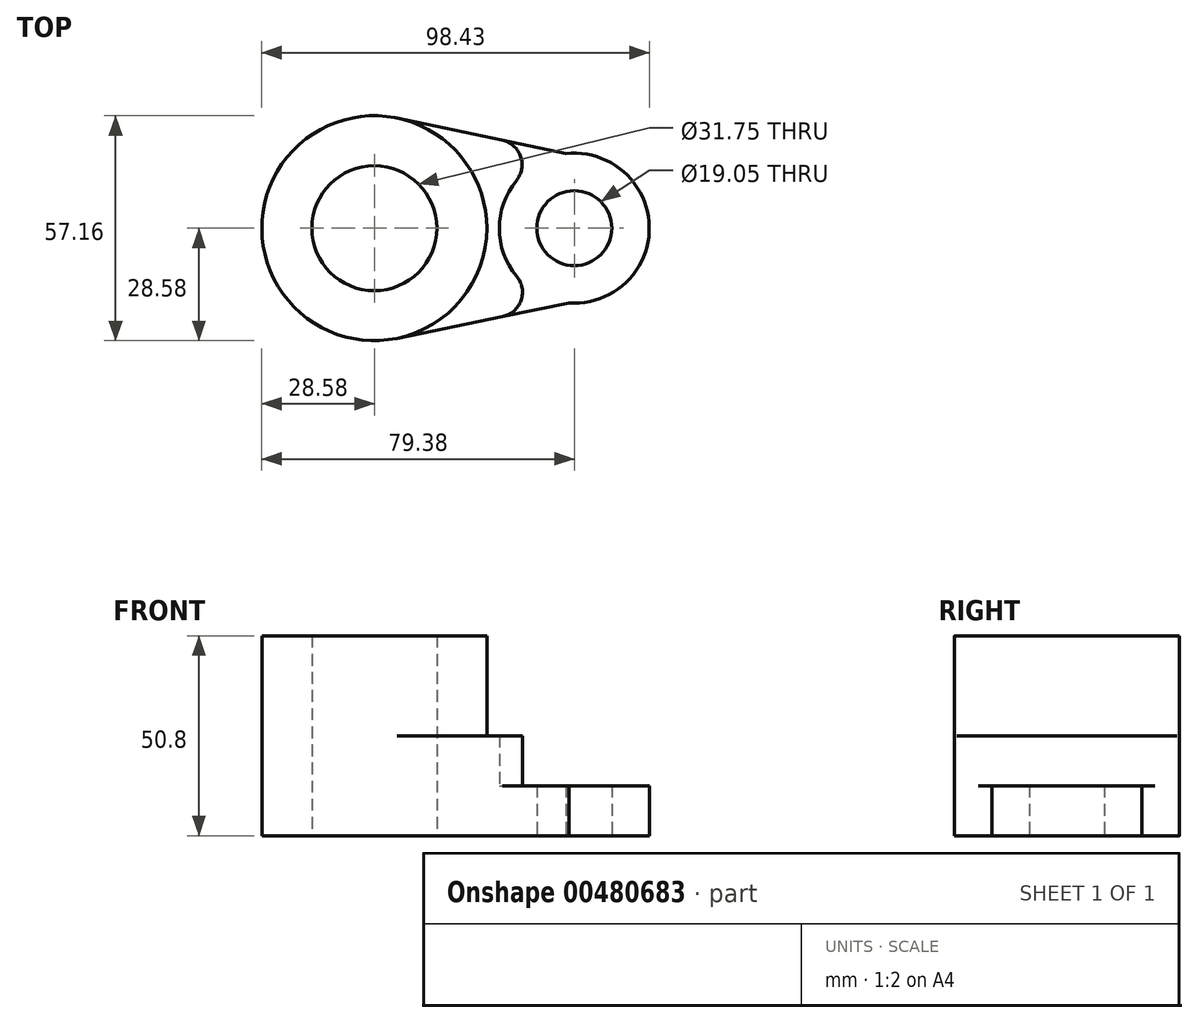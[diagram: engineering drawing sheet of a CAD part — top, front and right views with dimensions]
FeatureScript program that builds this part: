
annotation { "Feature Type Name" : "Feature", "Feature Type Description" : "" }
export const myFeature = defineFeature(function(context is Context, id is Id, definition is map)
    precondition{}
    {
        {
            var Q0;
            Q0=qCreatedBy(makeId("Top.planeOp"),FACE);
            var sketch = newSketch(context, id + "F0", { "sketchPlane" : qUnion([Q0])});
            skCircle(sketch, "E0", {"center": v(27.06, 0) * mm, "radius": 9.53 * mm});
            skCircle(sketch, "E1", {"center": v(27.06, 0) * mm, "radius": 19.05 * mm});
            skCircle(sketch, "E2", {"center": v(-23.74, 0) * mm, "radius": 15.88 * mm});
            skCircle(sketch, "E3", {"center": v(-23.74, 0) * mm, "radius": 28.58 * mm});
            skPoint(sketch, "E4", {"position": v(-14.86, 27.16) * mm});
            skPoint(sketch, "E5", {"position": v(24.93, 18.93) * mm});
            skLineSegment(sketch, "E6", {"start": v(-17.99, -27.99) * mm, "end": v(25.73, -19) * mm});
            skLineSegment(sketch, "E7", {"start": v(-17.84, 27.96) * mm, "end": v(24.93, 18.93) * mm});
            skSolve(sketch);
        }
        {
            var Q0;
            Q0=makeQuery(id+"F0.imprint","IMPRINT",FACE,{"disambiguationData":[TD([[makeQuery(id+"F0.imprint","IMPRINT",EDGE,{"derivedFrom":sQuery(id+"F0.wireOp",EDGE,"E2")}),-1.0]])]});
            extrude(context, id + "F1", {"entities" : qUnion([Q0]), "depth" : 50.8 * mm});
        }
        {
            var Q0;
            {var subQ0=sQuery(id+"F0.wireOp",EDGE,"E6");Q0=makeQuery(id+"F0.imprint","IMPRINT",FACE,{"disambiguationData":[TD([[makeQuery(id+"F0.imprint","IMPRINT",EDGE,{"derivedFrom":subQ0}),1.0]])]});}
            extrude(context, id + "F2", {"entities" : qUnion([Q0]), "operationType" : NewBodyOperationType.ADD, "depth" : 25.4 * mm});
        }
        {
            var Q0;
            Q0=makeQuery(id+"F0.imprint","IMPRINT",FACE,{"disambiguationData":[TD([[makeQuery(id+"F0.imprint","IMPRINT",EDGE,{"derivedFrom":sQuery(id+"F0.wireOp",EDGE,"E0")}),-1.0]])]});
            extrude(context, id + "F3", {"entities" : qUnion([Q0]), "operationType" : NewBodyOperationType.ADD, "depth" : 12.7 * mm});
        }
        {
            var Q0;
            {var subQ0=sQuery(id+"F0.wireOp",EDGE,"E1");var subQ1=sQuery(id+"F0.wireOp",EDGE,"E6");Q0=makeQuery(id+"F3.boolean.opBoolean","SPLIT",EDGE,{"disambiguationData":[topologyDisambiguationEdgeConnected([makeQuery(id+"F2.opExtrude","SWEPT_FACE",FACE,{"disambiguationData":[OSD([subQ0])]})])],"derivedFrom":makeQuery(id+"F2.opExtrude","SWEPT_EDGE",EDGE,{"disambiguationData":[OSD([subQ0,subQ1])]})});}
            var Q1;
            {var subQ0=sQuery(id+"F0.wireOp",EDGE,"E1");var subQ1=sQuery(id+"F0.wireOp",EDGE,"E7");Q1=makeQuery(id+"F3.boolean.opBoolean","SPLIT",EDGE,{"disambiguationData":[topologyDisambiguationEdgeConnected([makeQuery(id+"F2.opExtrude","SWEPT_FACE",FACE,{"disambiguationData":[OSD([subQ0])]})])],"derivedFrom":makeQuery(id+"F2.opExtrude","SWEPT_EDGE",EDGE,{"disambiguationData":[OSD([subQ0,subQ1])]})});}
            fillet(context, id + "F4", {"entities" : qUnion([Q0, Q1]), "radius" : 6.35 * mm, "tangentPropagation" : true, "allowEdgeOverflow" : false});
        }
    });
